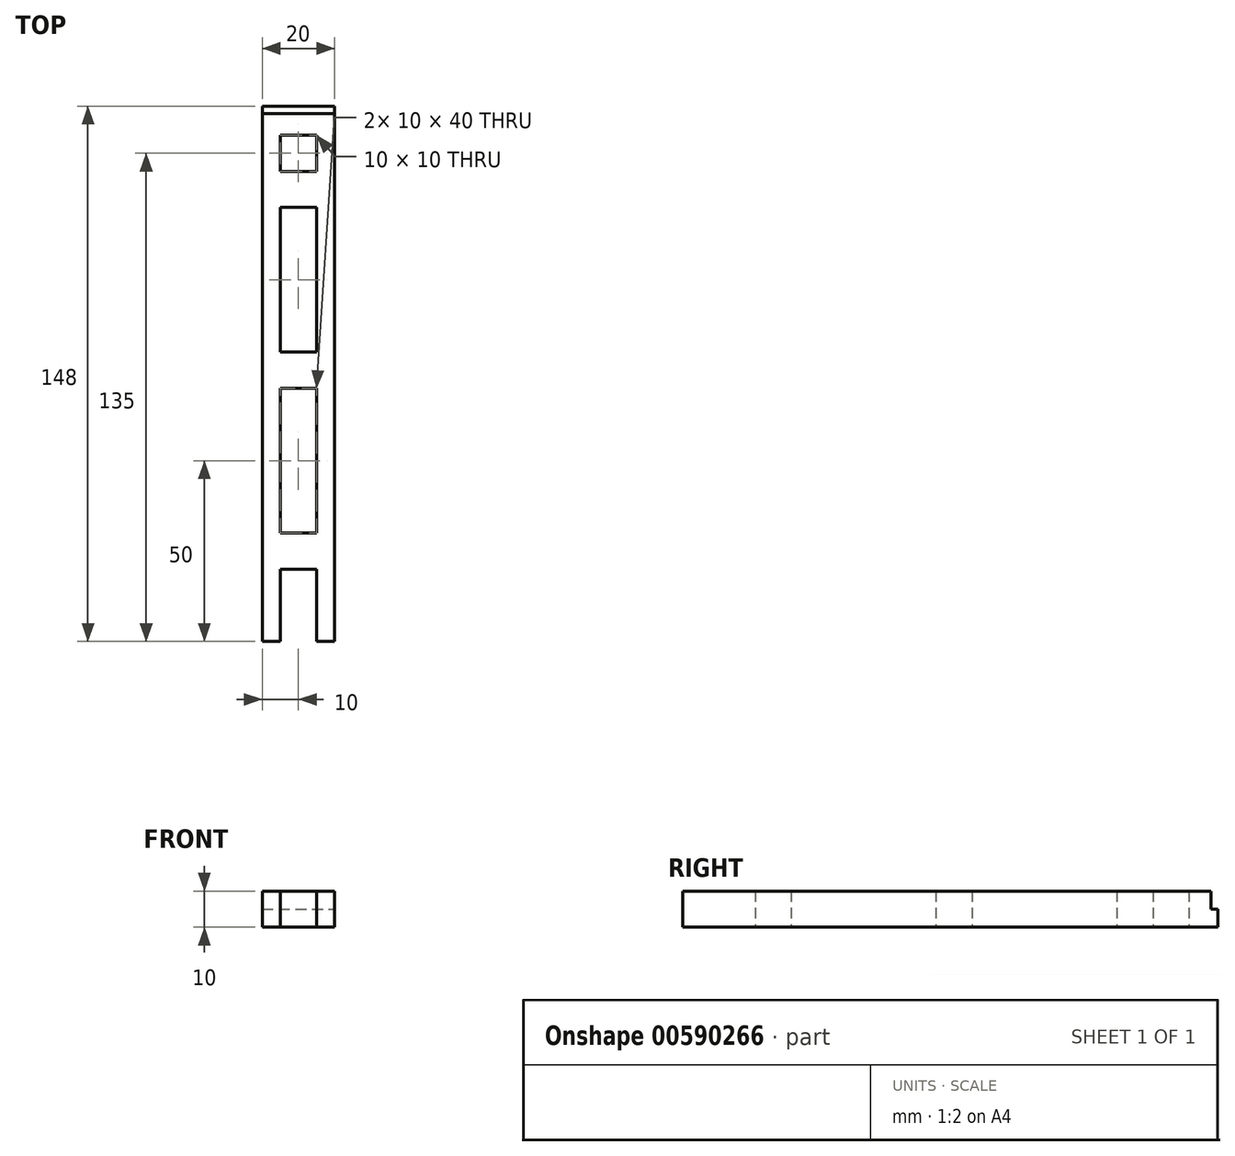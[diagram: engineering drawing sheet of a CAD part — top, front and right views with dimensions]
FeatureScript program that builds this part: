
annotation { "Feature Type Name" : "Feature", "Feature Type Description" : "" }
export const myFeature = defineFeature(function(context is Context, id is Id, definition is map)
    precondition{}
    {
        {
            var Q0;
            Q0=qCreatedBy(makeId("Top.planeOp"),FACE);
            var sketch = newSketch(context, id + "F0", { "sketchPlane" : qUnion([Q0])});
            skLineSegment(sketch, "E0.bottom", {"start": v(0, 0) * mm, "end": v(5, 0) * mm});
            skLineSegment(sketch, "E0.top", {"start": v(0, 140) * mm, "end": v(5, 140) * mm});
            skLineSegment(sketch, "E0.left", {"start": v(0, 0) * mm, "end": v(0, 140) * mm});
            skLineSegment(sketch, "E0.right", {"start": v(5, 0) * mm, "end": v(5, 140) * mm});
            skLineSegment(sketch, "E1.bottom", {"start": v(15, 0) * mm, "end": v(20, 0) * mm});
            skLineSegment(sketch, "E1.top", {"start": v(15, 140) * mm, "end": v(20, 140) * mm});
            skLineSegment(sketch, "E1.left", {"start": v(15, 0) * mm, "end": v(15, 140) * mm});
            skLineSegment(sketch, "E1.right", {"start": v(20, 0) * mm, "end": v(20, 140) * mm});
            skLineSegment(sketch, "E2.bottom", {"start": v(5, 20) * mm, "end": v(15, 20) * mm});
            skLineSegment(sketch, "E2.top", {"start": v(5, 30) * mm, "end": v(15, 30) * mm});
            skLineSegment(sketch, "E2.left", {"start": v(5, 20) * mm, "end": v(5, 30) * mm});
            skLineSegment(sketch, "E2.right", {"start": v(15, 20) * mm, "end": v(15, 30) * mm});
            skLineSegment(sketch, "E3.bottom", {"start": v(5, 70) * mm, "end": v(15, 70) * mm});
            skLineSegment(sketch, "E3.top", {"start": v(5, 80) * mm, "end": v(15, 80) * mm});
            skLineSegment(sketch, "E3.left", {"start": v(5, 70) * mm, "end": v(5, 80) * mm});
            skLineSegment(sketch, "E3.right", {"start": v(15, 70) * mm, "end": v(15, 80) * mm});
            skLineSegment(sketch, "E4.bottom", {"start": v(5, 120) * mm, "end": v(15, 120) * mm});
            skLineSegment(sketch, "E4.top", {"start": v(5, 130) * mm, "end": v(15, 130) * mm});
            skLineSegment(sketch, "E4.left", {"start": v(5, 120) * mm, "end": v(5, 130) * mm});
            skLineSegment(sketch, "E4.right", {"start": v(15, 120) * mm, "end": v(15, 130) * mm});
            skSolve(sketch);
        }
        {
            var Q0;
            Q0 = qSketchRegion(id + "F0", true);
            extrude(context, id + "F1", {"entities" : qUnion([Q0]), "depth" : 10 * mm, "offsetDistance" : 25 * mm});
        }
        {
            var Q0;
            Q0=qCreatedBy(makeId("Top.planeOp"),FACE);
            var sketch = newSketch(context, id + "F2", { "sketchPlane" : qUnion([Q0])});
            skLineSegment(sketch, "E5.bottom", {"start": v(5, 70) * mm, "end": v(15, 70) * mm});
            skLineSegment(sketch, "E5.top", {"start": v(5, 80) * mm, "end": v(15, 80) * mm});
            skLineSegment(sketch, "E5.left", {"start": v(5, 70) * mm, "end": v(5, 80) * mm});
            skLineSegment(sketch, "E5.right", {"start": v(15, 70) * mm, "end": v(15, 80) * mm});
            skSolve(sketch);
        }
        {
            var Q0;
            Q0 = qSketchRegion(id + "F2", true);
            extrude(context, id + "F3", {"entities" : qUnion([Q0]), "operationType" : NewBodyOperationType.ADD, "depth" : 10 * mm, "offsetDistance" : 25 * mm});
        }
        {
            var Q0;
            Q0=qCreatedBy(makeId("Top.planeOp"),FACE);
            var sketch = newSketch(context, id + "F4", { "sketchPlane" : qUnion([Q0])});
            skLineSegment(sketch, "E6.bottom", {"start": v(0, 140) * mm, "end": v(20, 140) * mm});
            skLineSegment(sketch, "E6.top", {"start": v(0, 148) * mm, "end": v(20, 148) * mm});
            skLineSegment(sketch, "E6.left", {"start": v(0, 140) * mm, "end": v(0, 148) * mm});
            skLineSegment(sketch, "E6.right", {"start": v(20, 140) * mm, "end": v(20, 148) * mm});
            skSolve(sketch);
        }
        {
            var Q0;
            Q0 = qSketchRegion(id + "F4", true);
            extrude(context, id + "F5", {"entities" : qUnion([Q0]), "operationType" : NewBodyOperationType.ADD, "depth" : 5 * mm, "offsetDistance" : 25 * mm});
        }
        {
            var Q0;
            Q0=makeQuery(id+"F5.opExtrude","CAP_FACE",FACE,{"disambiguationData":[OSD([sQuery(id+"F4.wireOp",EDGE,"E6.bottom"),sQuery(id+"F4.wireOp",EDGE,"E6.top"),sQuery(id+"F4.wireOp",EDGE,"E6.left"),sQuery(id+"F4.wireOp",EDGE,"E6.right")])],"isStart":false});
            var sketch = newSketch(context, id + "F6", { "sketchPlane" : qUnion([Q0])});
            skLineSegment(sketch, "E7.bottom", {"start": v(0, 140) * mm, "end": v(20, 140) * mm});
            skLineSegment(sketch, "E7.top", {"start": v(0, 146) * mm, "end": v(20, 146) * mm});
            skLineSegment(sketch, "E7.left", {"start": v(0, 140) * mm, "end": v(0, 146) * mm});
            skLineSegment(sketch, "E7.right", {"start": v(20, 140) * mm, "end": v(20, 146) * mm});
            skSolve(sketch);
        }
        {
            var Q0;
            Q0 = qSketchRegion(id + "F6", true);
            extrude(context, id + "F7", {"entities" : qUnion([Q0]), "operationType" : NewBodyOperationType.ADD, "depth" : 5 * mm, "offsetDistance" : 25 * mm});
        }
    });
